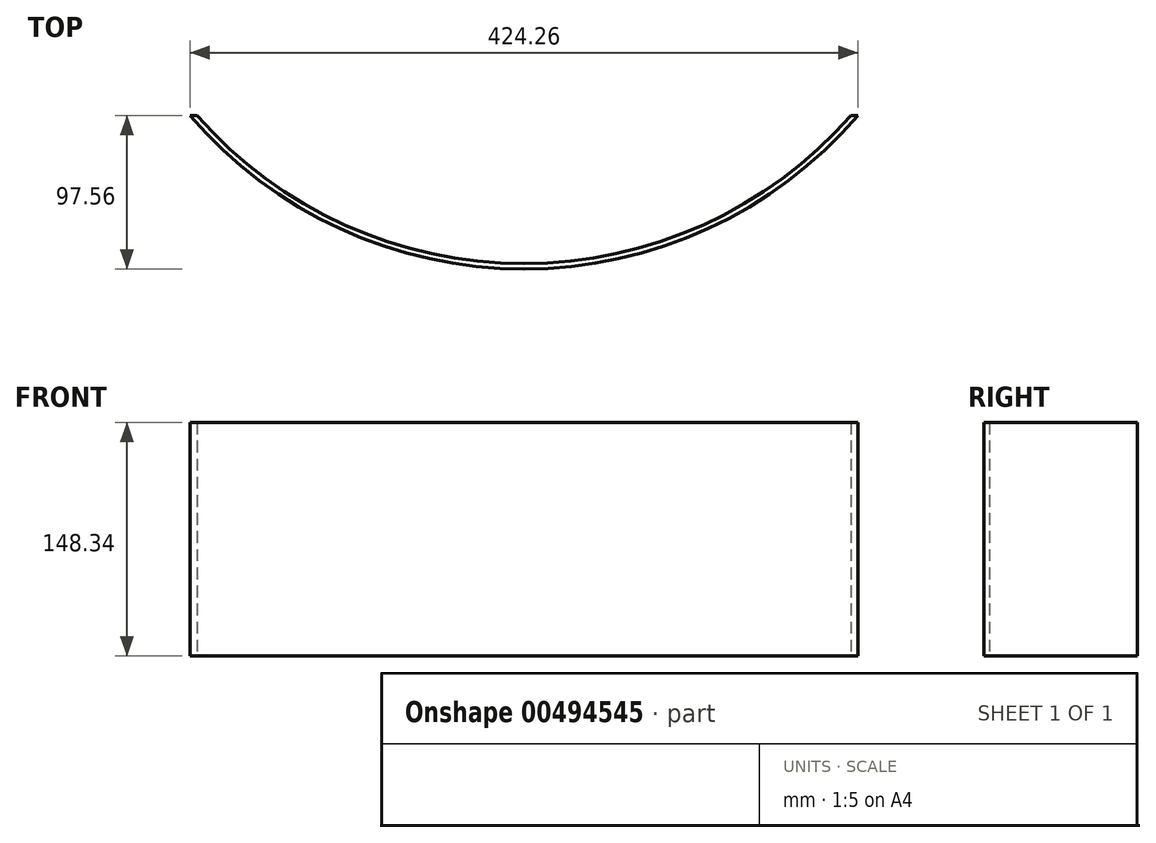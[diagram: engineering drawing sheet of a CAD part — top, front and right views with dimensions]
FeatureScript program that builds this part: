
annotation { "Feature Type Name" : "Feature", "Feature Type Description" : "" }
export const myFeature = defineFeature(function(context is Context, id is Id, definition is map)
    precondition{}
    {
        {
            var Q0;
            Q0=qCreatedBy(makeId("Top.planeOp"),FACE);
            var sketch = newSketch(context, id + "F0", { "sketchPlane" : qUnion([Q0])});
            skCircle(sketch, "E0", {"center": v(0, 0) * mm, "radius": 279.4 * mm});
            skCircle(sketch, "E1", {"center": v(0, 0) * mm, "radius": 275.97 * mm});
            skSolve(sketch);
        }
        {
            var Q0;
            Q0=qSketchRegion(id+"F0",true);
            extrude(context, id + "F1", {"entities" : qUnion([Q0]), "depth" : 148.34 * mm});
        }
        {
            var Q0;
            Q0=qCreatedBy(makeId("Top.planeOp"),FACE);
            var sketch = newSketch(context, id + "F2", { "sketchPlane" : qUnion([Q0])});
            skLineSegment(sketch, "E2.bottom", {"start": v(-292.68, -181.84) * mm, "end": v(301.33, -181.84) * mm});
            skLineSegment(sketch, "E2.top", {"start": v(-292.68, 280.28) * mm, "end": v(301.33, 280.28) * mm});
            skLineSegment(sketch, "E2.left", {"start": v(-292.68, -181.84) * mm, "end": v(-292.68, 280.28) * mm});
            skLineSegment(sketch, "E2.right", {"start": v(301.33, -181.84) * mm, "end": v(301.33, 280.28) * mm});
            skSolve(sketch);
        }
        {
            var Q0;
            Q0 = qSketchRegion(id + "F2", true);
            extrude(context, id + "F3", {"entities" : qUnion([Q0]), "operationType" : NewBodyOperationType.REMOVE, "endBound" : BoundingType.THROUGH_ALL, "depth" : 1397 * mm});
        }
    });
